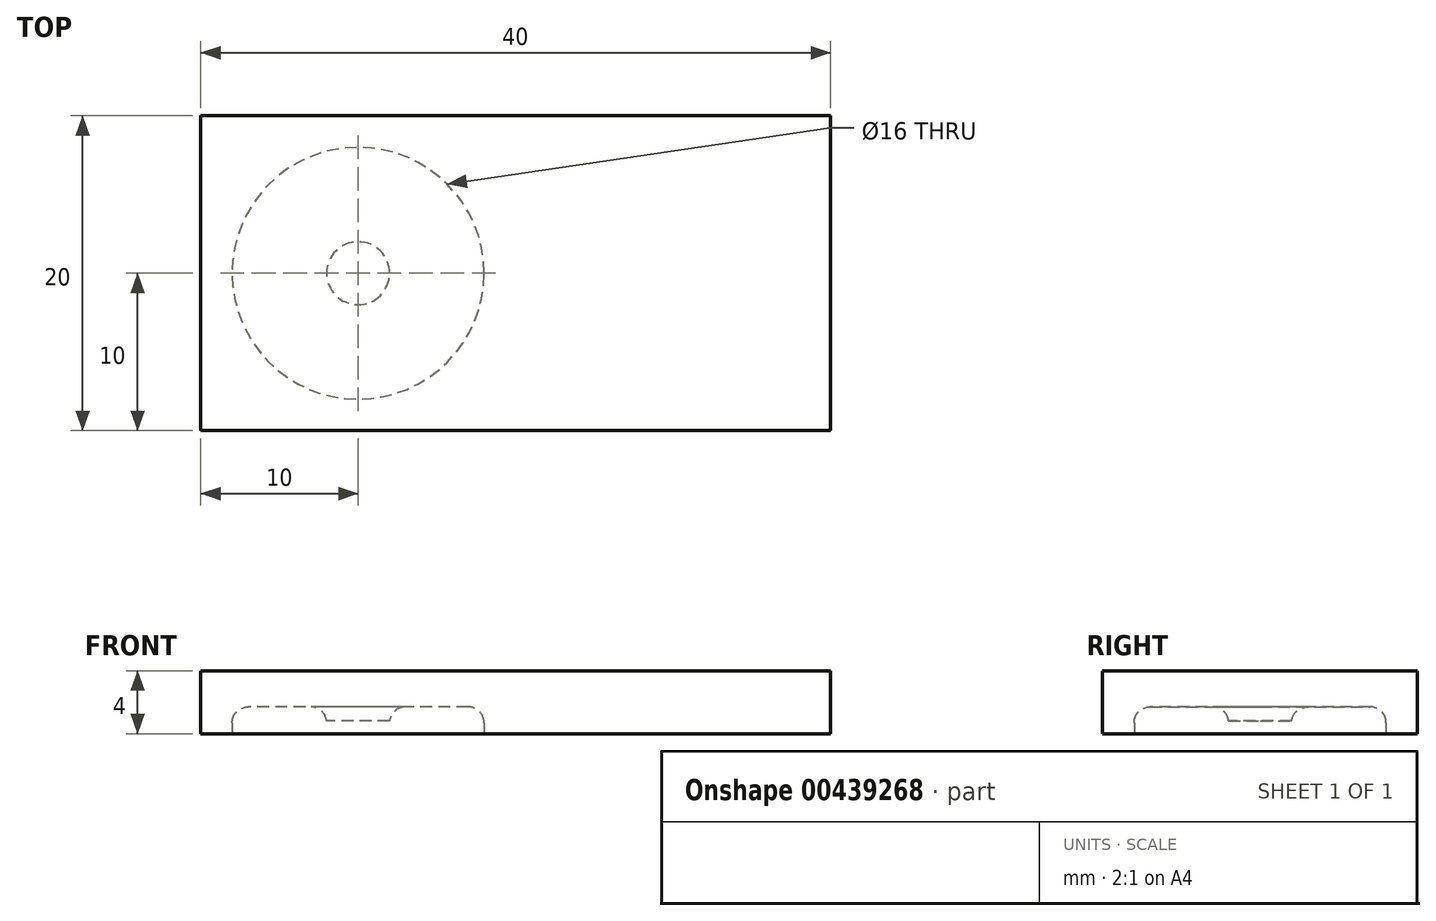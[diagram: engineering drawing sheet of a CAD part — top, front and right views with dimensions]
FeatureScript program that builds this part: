
annotation { "Feature Type Name" : "Feature", "Feature Type Description" : "" }
export const myFeature = defineFeature(function(context is Context, id is Id, definition is map)
    precondition{}
    {
        {
            var Q0;
            Q0=qCreatedBy(makeId("Top.planeOp"),FACE);
            var sketch = newSketch(context, id + "F0", { "sketchPlane" : qUnion([Q0])});
            skLineSegment(sketch, "E0.bottom", {"start": v(0, 0) * mm, "end": v(20, 0) * mm});
            skLineSegment(sketch, "E0.top", {"start": v(0, 20) * mm, "end": v(20, 20) * mm});
            skLineSegment(sketch, "E0.left", {"start": v(0, 0) * mm, "end": v(0, 20) * mm});
            skLineSegment(sketch, "E0.right", {"start": v(20, 0) * mm, "end": v(20, 20) * mm});
            skCircle(sketch, "E1", {"center": v(10, 10) * mm, "radius": 8 * mm});
            skCircle(sketch, "E2", {"center": v(10, 10) * mm, "radius": 2 * mm});
            skSolve(sketch);
        }
        {
            var Q0;
            Q0=makeQuery(id+"F0.imprint","IMPRINT",FACE,{"disambiguationData":[TD([[makeQuery(id+"F0.imprint","IMPRINT",EDGE,{"derivedFrom":sQuery(id+"F0.wireOp",EDGE,"E0.bottom")}),1.0]])]});
            var Q1;
            Q1=makeQuery(id+"F0.imprint","IMPRINT",FACE,{"disambiguationData":[TD([[makeQuery(id+"F0.imprint","IMPRINT",EDGE,{"derivedFrom":sQuery(id+"F0.wireOp",EDGE,"E1")}),1.0]])]});
            var Q2;
            Q2=makeQuery(id+"F0.imprint","IMPRINT",FACE,{"disambiguationData":[TD([[makeQuery(id+"F0.imprint","IMPRINT",EDGE,{"derivedFrom":sQuery(id+"F0.wireOp",EDGE,"E2")}),1.0]])]});
            extrude(context, id + "F1", {"entities" : qUnion([Q0, Q1, Q2]), "depth" : 4 * mm});
        }
        {
            var Q0;
            Q0=makeQuery(id+"F0.imprint","IMPRINT",FACE,{"disambiguationData":[TD([[makeQuery(id+"F0.imprint","IMPRINT",EDGE,{"derivedFrom":sQuery(id+"F0.wireOp",EDGE,"E1")}),1.0]])]});
            extrude(context, id + "F2", {"entities" : qUnion([Q0]), "operationType" : NewBodyOperationType.REMOVE, "depth" : 1.7 * mm});
        }
        {
            var Q0;
            Q0=makeQuery(id+"F0.imprint","IMPRINT",FACE,{"disambiguationData":[TD([[makeQuery(id+"F0.imprint","IMPRINT",EDGE,{"derivedFrom":sQuery(id+"F0.wireOp",EDGE,"E2")}),1.0]])]});
            extrude(context, id + "F3", {"entities" : qUnion([Q0]), "operationType" : NewBodyOperationType.REMOVE, "depth" : 0.8 * mm});
        }
        {
            var Q0;
            Q0=makeQuery(id+"F2.boolean.opBoolean","COPY",EDGE,{"derivedFrom":makeQuery(id+"F2.opExtrude","CAP_EDGE",EDGE,{"disambiguationData":[OSD([sQuery(id+"F0.wireOp",EDGE,"E1")])],"isStart":false})});
            var Q1;
            Q1=makeQuery(id+"F2.boolean.opBoolean","COPY",EDGE,{"derivedFrom":makeQuery(id+"F2.opExtrude","CAP_EDGE",EDGE,{"disambiguationData":[OSD([sQuery(id+"F0.wireOp",EDGE,"E2")])],"isStart":false})});
            fillet(context, id + "F4", {"entities" : qUnion([Q0, Q1]), "radius" : 1 * mm, "tangentPropagation" : true, "allowEdgeOverflow" : false});
        }
        {
            var Q0;
            Q0=makeQuery(id+"F1.opExtrude","SWEPT_FACE",FACE,{"disambiguationData":[OSD([sQuery(id+"F0.wireOp",EDGE,"E0.right")])]});
            extrude(context, id + "F5", {"entities" : qUnion([Q0]), "operationType" : NewBodyOperationType.ADD, "depth" : 20 * mm});
        }
    });
